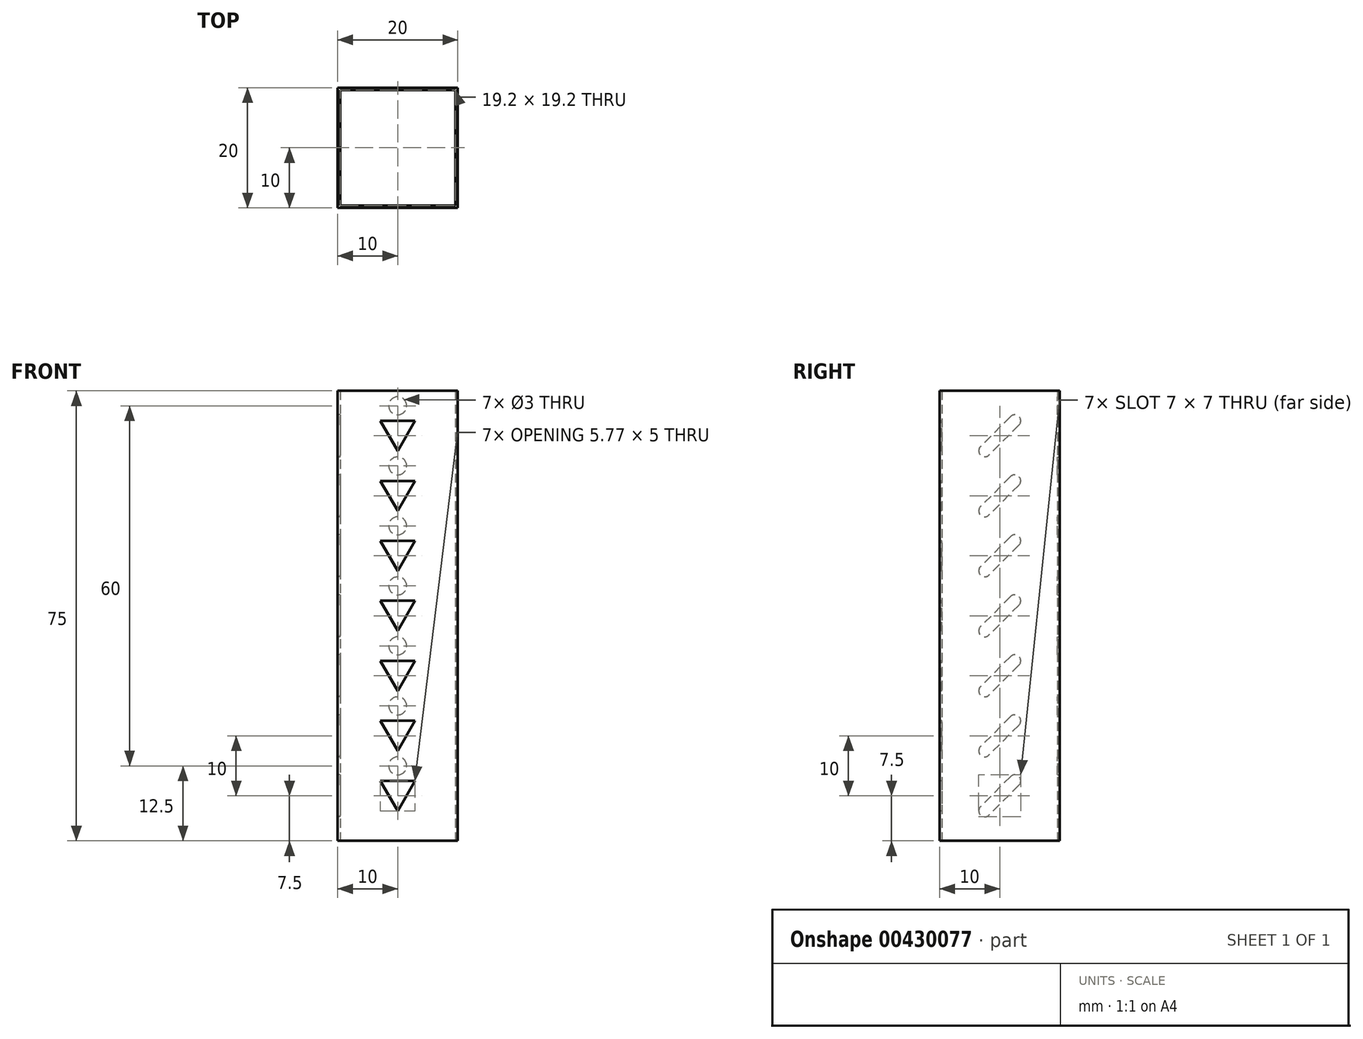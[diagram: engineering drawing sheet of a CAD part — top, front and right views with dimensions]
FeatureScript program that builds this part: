
annotation { "Feature Type Name" : "Feature", "Feature Type Description" : "" }
export const myFeature = defineFeature(function(context is Context, id is Id, definition is map)
    precondition{}
    {
        {
            var Q0;
            Q0=qCreatedBy(makeId("Top.planeOp"),FACE);
            var sketch = newSketch(context, id + "F0", { "sketchPlane" : qUnion([Q0])});
            skLineSegment(sketch, "E0.bottom", {"start": v(10, 10) * mm, "end": v(-10, 10) * mm});
            skLineSegment(sketch, "E0.top", {"start": v(10, -10) * mm, "end": v(-10, -10) * mm});
            skLineSegment(sketch, "E0.left", {"start": v(10, 10) * mm, "end": v(10, -10) * mm});
            skLineSegment(sketch, "E0.right", {"start": v(-10, 10) * mm, "end": v(-10, -10) * mm});
            skPoint(sketch, "E0.middle", {"position": v(0, 0) * mm});
            skLineSegment(sketch, "E1.bottom", {"start": v(9.6, 9.6) * mm, "end": v(-9.6, 9.6) * mm});
            skLineSegment(sketch, "E1.top", {"start": v(9.6, -9.6) * mm, "end": v(-9.6, -9.6) * mm});
            skLineSegment(sketch, "E1.left", {"start": v(9.6, 9.6) * mm, "end": v(9.6, -9.6) * mm});
            skLineSegment(sketch, "E1.right", {"start": v(-9.6, 9.6) * mm, "end": v(-9.6, -9.6) * mm});
            skSolve(sketch);
        }
        {
            var Q0;
            Q0=qSketchRegion(id+"F0",true);
            extrude(context, id + "F1", {"entities" : qUnion([Q0]), "depth" : (10 * 7 + 5) * mm});
        }
        {
            var Q0;
            Q0=makeQuery(id+"F1.opExtrude","SWEPT_FACE",FACE,{"disambiguationData":[OSD([sQuery(id+"F0.wireOp",EDGE,"E0.bottom")])]});
            var sketch = newSketch(context, id + "F2", { "sketchPlane" : qUnion([Q0])});
            skCircle(sketch, "E2", {"center": v(0, 62.5) * mm, "radius": 1.5 * mm});
            skCircle(sketch, "E3", {"center": v(0, 52.5) * mm, "radius": 1.5 * mm});
            skCircle(sketch, "E4", {"center": v(0, 42.5) * mm, "radius": 1.5 * mm});
            skCircle(sketch, "E5", {"center": v(0, 32.5) * mm, "radius": 1.5 * mm});
            skCircle(sketch, "E6", {"center": v(0, 22.5) * mm, "radius": 1.5 * mm});
            skCircle(sketch, "E7", {"center": v(0, 12.5) * mm, "radius": 1.5 * mm});
            skCircle(sketch, "E8", {"center": v(0, 72.5) * mm, "radius": 1.5 * mm});
            skSolve(sketch);
        }
        {
            var Q0;
            Q0=makeQuery(id+"F2.imprint","IMPRINT",FACE,{"disambiguationData":[TD([[makeQuery(id+"F2.imprint","IMPRINT",EDGE,{"derivedFrom":sQuery(id+"F2.wireOp",EDGE,"E2")}),1.0]])]});
            var Q1;
            Q1=makeQuery(id+"F2.imprint","IMPRINT",FACE,{"disambiguationData":[TD([[makeQuery(id+"F2.imprint","IMPRINT",EDGE,{"derivedFrom":sQuery(id+"F2.wireOp",EDGE,"E3")}),1.0]])]});
            var Q2;
            Q2=makeQuery(id+"F2.imprint","IMPRINT",FACE,{"disambiguationData":[TD([[makeQuery(id+"F2.imprint","IMPRINT",EDGE,{"derivedFrom":sQuery(id+"F2.wireOp",EDGE,"E4")}),1.0]])]});
            var Q3;
            Q3=makeQuery(id+"F2.imprint","IMPRINT",FACE,{"disambiguationData":[TD([[makeQuery(id+"F2.imprint","IMPRINT",EDGE,{"derivedFrom":sQuery(id+"F2.wireOp",EDGE,"E5")}),1.0]])]});
            var Q4;
            Q4=makeQuery(id+"F2.imprint","IMPRINT",FACE,{"disambiguationData":[TD([[makeQuery(id+"F2.imprint","IMPRINT",EDGE,{"derivedFrom":sQuery(id+"F2.wireOp",EDGE,"E6")}),1.0]])]});
            var Q5;
            Q5=makeQuery(id+"F2.imprint","IMPRINT",FACE,{"disambiguationData":[TD([[makeQuery(id+"F2.imprint","IMPRINT",EDGE,{"derivedFrom":sQuery(id+"F2.wireOp",EDGE,"E7")}),1.0]])]});
            var Q6;
            Q6=makeQuery(id+"F2.imprint","IMPRINT",FACE,{"disambiguationData":[TD([[makeQuery(id+"F2.imprint","IMPRINT",EDGE,{"derivedFrom":sQuery(id+"F2.wireOp",EDGE,"E8")}),1.0]])]});
            extrude(context, id + "F3", {"entities" : qUnion([Q0, Q1, Q2, Q3, Q4, Q5, Q6]), "operationType" : NewBodyOperationType.REMOVE, "endBound" : BoundingType.UP_TO_NEXT, "oppositeDirection" : true, "depth" : 25 * mm});
        }
        {
            var Q0;
            Q0=makeQuery(id+"F1.opExtrude","SWEPT_FACE",FACE,{"disambiguationData":[OSD([sQuery(id+"F0.wireOp",EDGE,"E0.top")])]});
            var sketch = newSketch(context, id + "F4", { "sketchPlane" : qUnion([Q0])});
            skLineSegment(sketch, "E9", {"start": v(-2.89, 10) * mm, "end": v(0, 5) * mm});
            skLineSegment(sketch, "E10", {"start": v(0, 5) * mm, "end": v(2.89, 10) * mm});
            skLineSegment(sketch, "E11", {"start": v(2.89, 10) * mm, "end": v(-2.89, 10) * mm});
            skLineSegment(sketch, "E12.1.0.0", {"start": v(0, 15) * mm, "end": v(2.89, 20) * mm});
            skLineSegment(sketch, "E12.1.0.1", {"start": v(2.89, 20) * mm, "end": v(-2.89, 20) * mm});
            skLineSegment(sketch, "E12.1.0.2", {"start": v(-2.89, 20) * mm, "end": v(0, 15) * mm});
            skLineSegment(sketch, "E12.2.0.0", {"start": v(0, 25) * mm, "end": v(2.89, 30) * mm});
            skLineSegment(sketch, "E12.2.0.1", {"start": v(2.89, 30) * mm, "end": v(-2.89, 30) * mm});
            skLineSegment(sketch, "E12.2.0.2", {"start": v(-2.89, 30) * mm, "end": v(0, 25) * mm});
            skLineSegment(sketch, "E12.3.0.0", {"start": v(0, 35) * mm, "end": v(2.89, 40) * mm});
            skLineSegment(sketch, "E12.3.0.1", {"start": v(2.89, 40) * mm, "end": v(-2.89, 40) * mm});
            skLineSegment(sketch, "E12.3.0.2", {"start": v(-2.89, 40) * mm, "end": v(0, 35) * mm});
            skLineSegment(sketch, "E12.4.0.0", {"start": v(0, 45) * mm, "end": v(2.89, 50) * mm});
            skLineSegment(sketch, "E12.4.0.1", {"start": v(2.89, 50) * mm, "end": v(-2.89, 50) * mm});
            skLineSegment(sketch, "E12.4.0.2", {"start": v(-2.89, 50) * mm, "end": v(0, 45) * mm});
            skLineSegment(sketch, "E12.5.0.0", {"start": v(0, 55) * mm, "end": v(2.89, 60) * mm});
            skLineSegment(sketch, "E12.5.0.1", {"start": v(2.89, 60) * mm, "end": v(-2.89, 60) * mm});
            skLineSegment(sketch, "E12.5.0.2", {"start": v(-2.89, 60) * mm, "end": v(0, 55) * mm});
            skLineSegment(sketch, "E12.6.0.0", {"start": v(0, 65) * mm, "end": v(2.89, 70) * mm});
            skLineSegment(sketch, "E12.6.0.1", {"start": v(2.89, 70) * mm, "end": v(-2.89, 70) * mm});
            skLineSegment(sketch, "E12.6.0.2", {"start": v(-2.89, 70) * mm, "end": v(0, 65) * mm});
            skLineSegment(sketch, "E12.direction1", {"start": v(0, 5) * mm, "end": v(0, 15) * mm, "construction": true});
            skSolve(sketch);
        }
        {
            var Q0;
            Q0 = qSketchRegion(id + "F4", true);
            extrude(context, id + "F5", {"entities" : qUnion([Q0]), "operationType" : NewBodyOperationType.REMOVE, "endBound" : BoundingType.UP_TO_NEXT, "oppositeDirection" : true, "depth" : 25 * mm});
        }
        {
            var Q0;
            Q0=makeQuery(id+"F1.opExtrude","SWEPT_FACE",FACE,{"disambiguationData":[OSD([sQuery(id+"F0.wireOp",EDGE,"E0.right")])]});
            var sketch = newSketch(context, id + "F6", { "sketchPlane" : qUnion([Q0])});
            skLineSegment(sketch, "E13", {"start": v(-2.5, 10) * mm, "end": v(2.5, 5) * mm, "construction": true});
            skLineSegment(sketch, "E14", {"start": v(2.5, 5) * mm, "end": v(0, 7.5) * mm, "construction": true});
            skPoint(sketch, "E14.endSnap0", {"position": v(0, 7.5) * mm});
            skArc(sketch, "E15.0.startCap", {"start": v(-3.2, 9.3) * mm, "mid": v(-3.2, 10.7) * mm, "end": v(-1.8, 10.7) * mm});
            skArc(sketch, "E15.0.endCap", {"start": v(3.2, 5.7) * mm, "mid": v(3.2, 4.3) * mm, "end": v(1.8, 4.3) * mm});
            skLineSegment(sketch, "E15.0.left", {"start": v(-1.8, 10.7) * mm, "end": v(3.2, 5.7) * mm});
            skLineSegment(sketch, "E15.0.right", {"start": v(-3.2, 9.3) * mm, "end": v(1.8, 4.3) * mm});
            skLineSegment(sketch, "E16.1.0.0", {"start": v(-2.5, 20) * mm, "end": v(2.5, 15) * mm, "construction": true});
            skArc(sketch, "E16.1.0.1", {"start": v(-3.2, 19.3) * mm, "mid": v(-3.2, 20.7) * mm, "end": v(-1.8, 20.7) * mm});
            skLineSegment(sketch, "E16.1.0.2", {"start": v(-3.2, 19.3) * mm, "end": v(1.8, 14.3) * mm});
            skLineSegment(sketch, "E16.1.0.3", {"start": v(-1.8, 20.7) * mm, "end": v(3.2, 15.7) * mm});
            skLineSegment(sketch, "E16.1.0.4", {"start": v(2.5, 15) * mm, "end": v(0, 17.5) * mm, "construction": true});
            skPoint(sketch, "E16.1.0.5", {"position": v(0, 17.5) * mm});
            skArc(sketch, "E16.1.0.6", {"start": v(3.2, 15.7) * mm, "mid": v(3.2, 14.3) * mm, "end": v(1.8, 14.3) * mm});
            skLineSegment(sketch, "E16.2.0.0", {"start": v(-2.5, 30) * mm, "end": v(2.5, 25) * mm, "construction": true});
            skArc(sketch, "E16.2.0.1", {"start": v(-3.2, 29.3) * mm, "mid": v(-3.2, 30.7) * mm, "end": v(-1.8, 30.7) * mm});
            skLineSegment(sketch, "E16.2.0.2", {"start": v(-3.2, 29.3) * mm, "end": v(1.8, 24.3) * mm});
            skLineSegment(sketch, "E16.2.0.3", {"start": v(-1.8, 30.7) * mm, "end": v(3.2, 25.7) * mm});
            skLineSegment(sketch, "E16.2.0.4", {"start": v(2.5, 25) * mm, "end": v(0, 27.5) * mm, "construction": true});
            skPoint(sketch, "E16.2.0.5", {"position": v(0, 27.5) * mm});
            skArc(sketch, "E16.2.0.6", {"start": v(3.2, 25.7) * mm, "mid": v(3.2, 24.3) * mm, "end": v(1.8, 24.3) * mm});
            skLineSegment(sketch, "E16.3.0.0", {"start": v(-2.5, 40) * mm, "end": v(2.5, 35) * mm, "construction": true});
            skArc(sketch, "E16.3.0.1", {"start": v(-3.2, 39.3) * mm, "mid": v(-3.2, 40.7) * mm, "end": v(-1.8, 40.7) * mm});
            skLineSegment(sketch, "E16.3.0.2", {"start": v(-3.2, 39.3) * mm, "end": v(1.8, 34.3) * mm});
            skLineSegment(sketch, "E16.3.0.3", {"start": v(-1.8, 40.7) * mm, "end": v(3.2, 35.7) * mm});
            skLineSegment(sketch, "E16.3.0.4", {"start": v(2.5, 35) * mm, "end": v(0, 37.5) * mm, "construction": true});
            skPoint(sketch, "E16.3.0.5", {"position": v(0, 37.5) * mm});
            skArc(sketch, "E16.3.0.6", {"start": v(3.2, 35.7) * mm, "mid": v(3.2, 34.3) * mm, "end": v(1.8, 34.3) * mm});
            skLineSegment(sketch, "E16.4.0.0", {"start": v(-2.5, 50) * mm, "end": v(2.5, 45) * mm, "construction": true});
            skArc(sketch, "E16.4.0.1", {"start": v(-3.2, 49.3) * mm, "mid": v(-3.2, 50.7) * mm, "end": v(-1.8, 50.7) * mm});
            skLineSegment(sketch, "E16.4.0.2", {"start": v(-3.2, 49.3) * mm, "end": v(1.8, 44.3) * mm});
            skLineSegment(sketch, "E16.4.0.3", {"start": v(-1.8, 50.7) * mm, "end": v(3.2, 45.7) * mm});
            skLineSegment(sketch, "E16.4.0.4", {"start": v(2.5, 45) * mm, "end": v(0, 47.5) * mm, "construction": true});
            skPoint(sketch, "E16.4.0.5", {"position": v(0, 47.5) * mm});
            skArc(sketch, "E16.4.0.6", {"start": v(3.2, 45.7) * mm, "mid": v(3.2, 44.3) * mm, "end": v(1.8, 44.3) * mm});
            skLineSegment(sketch, "E16.5.0.0", {"start": v(-2.5, 60) * mm, "end": v(2.5, 55) * mm, "construction": true});
            skArc(sketch, "E16.5.0.1", {"start": v(-3.2, 59.3) * mm, "mid": v(-3.2, 60.7) * mm, "end": v(-1.8, 60.7) * mm});
            skLineSegment(sketch, "E16.5.0.2", {"start": v(-3.2, 59.3) * mm, "end": v(1.8, 54.3) * mm});
            skLineSegment(sketch, "E16.5.0.3", {"start": v(-1.8, 60.7) * mm, "end": v(3.2, 55.7) * mm});
            skLineSegment(sketch, "E16.5.0.4", {"start": v(2.5, 55) * mm, "end": v(0, 57.5) * mm, "construction": true});
            skPoint(sketch, "E16.5.0.5", {"position": v(0, 57.5) * mm});
            skArc(sketch, "E16.5.0.6", {"start": v(3.2, 55.7) * mm, "mid": v(3.2, 54.3) * mm, "end": v(1.8, 54.3) * mm});
            skLineSegment(sketch, "E16.6.0.0", {"start": v(-2.5, 70) * mm, "end": v(2.5, 65) * mm, "construction": true});
            skArc(sketch, "E16.6.0.1", {"start": v(-3.2, 69.3) * mm, "mid": v(-3.2, 70.7) * mm, "end": v(-1.8, 70.7) * mm});
            skLineSegment(sketch, "E16.6.0.2", {"start": v(-3.2, 69.3) * mm, "end": v(1.8, 64.3) * mm});
            skLineSegment(sketch, "E16.6.0.3", {"start": v(-1.8, 70.7) * mm, "end": v(3.2, 65.7) * mm});
            skLineSegment(sketch, "E16.6.0.4", {"start": v(2.5, 65) * mm, "end": v(0, 67.5) * mm, "construction": true});
            skPoint(sketch, "E16.6.0.5", {"position": v(0, 67.5) * mm});
            skArc(sketch, "E16.6.0.6", {"start": v(3.2, 65.7) * mm, "mid": v(3.2, 64.3) * mm, "end": v(1.8, 64.3) * mm});
            skLineSegment(sketch, "E16.direction1", {"start": v(0, 7.5) * mm, "end": v(0, 17.5) * mm, "construction": true});
            skSolve(sketch);
        }
        {
            var Q0;
            Q0 = qSketchRegion(id + "F6", true);
            extrude(context, id + "F7", {"entities" : qUnion([Q0]), "operationType" : NewBodyOperationType.REMOVE, "endBound" : BoundingType.UP_TO_NEXT, "oppositeDirection" : true, "depth" : 25 * mm});
        }
    });
